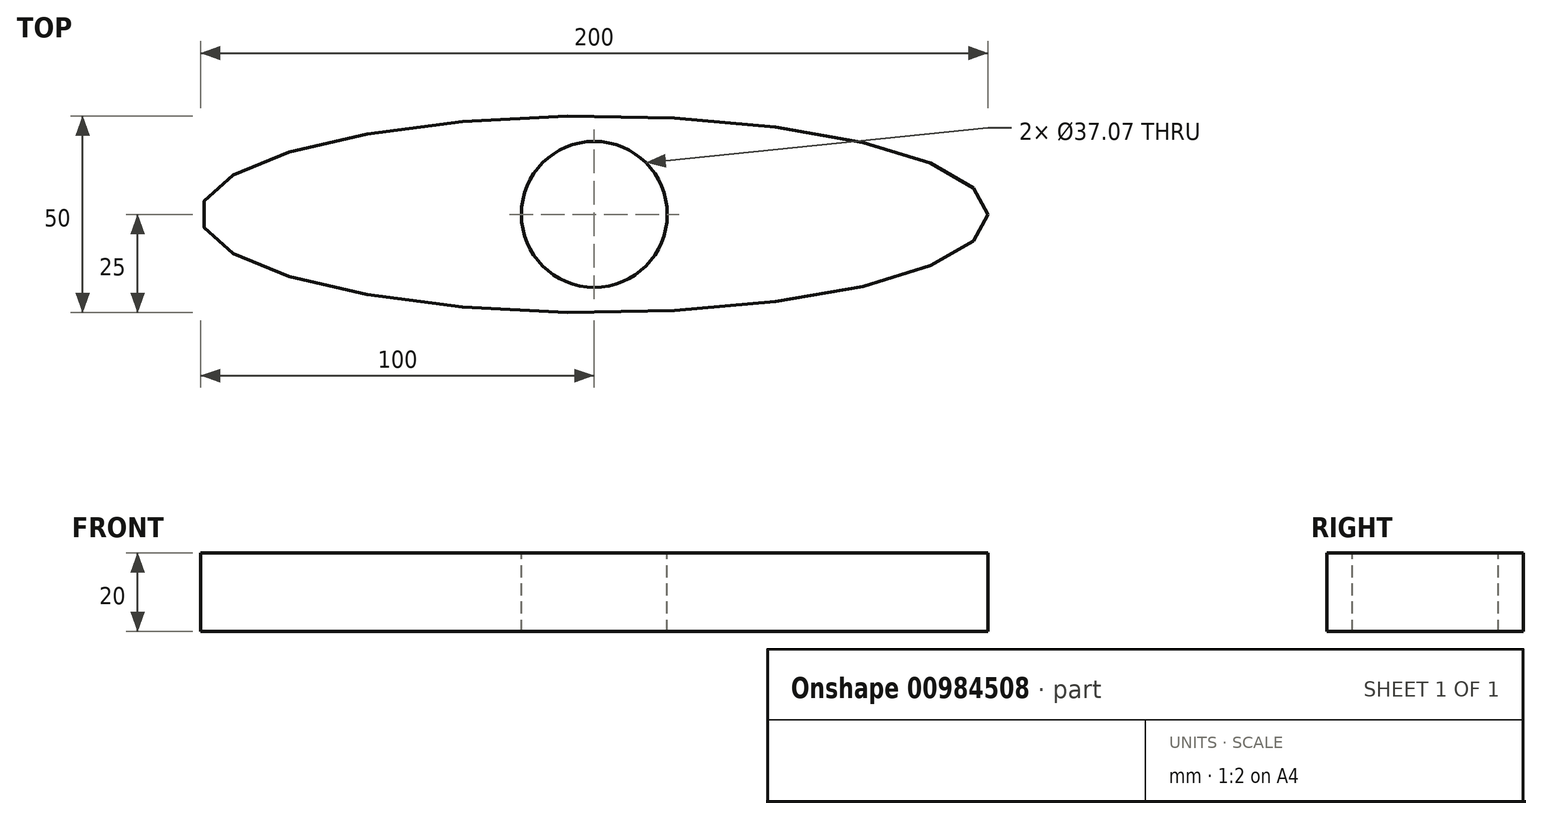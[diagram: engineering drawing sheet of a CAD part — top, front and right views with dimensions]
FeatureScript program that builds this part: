
annotation { "Feature Type Name" : "Feature", "Feature Type Description" : "" }
export const myFeature = defineFeature(function(context is Context, id is Id, definition is map)
    precondition{}
    {
        {
            var Q0;
            Q0=qCreatedBy(makeId("Top.planeOp"),FACE);
            var sketch = newSketch(context, id + "F0", { "sketchPlane" : qUnion([Q0])});
            skEllipse(sketch, "E0", {"center": v(0, 0) * mm, "majorRadius": 100 * mm, "minorRadius": 25 * mm, "majorAxis": v(1, 0)});
            skSolve(sketch);
        }
        {
            var Q0;
            Q0 = qSketchRegion(id + "F0", false);
            extrude(context, id + "F1", {"entities" : qUnion([Q0]), "depth" : 20 * mm});
        }
        {
            var Q0;
            Q0=qCreatedBy(makeId("Top.planeOp"),FACE);
            var sketch = newSketch(context, id + "F2", { "sketchPlane" : qUnion([Q0])});
            skEllipse(sketch, "E1", {"center": v(0, 0) * mm, "majorRadius": 100 * mm, "minorRadius": 25 * mm, "majorAxis": v(1, 0)});
            skSolve(sketch);
        }
        {
            var Q0;
            Q0 = qSketchRegion(id + "F2", false);
            extrude(context, id + "F3", {"entities" : qUnion([Q0]), "depth" : 20 * mm});
        }
        {
            var Q0;
            Q0=makeQuery(id+"F1.opExtrude","CAP_FACE",FACE,{"disambiguationData":[OSD([sQuery(id+"F0.wireOp",EDGE,"E0")])],"isStart":false});
            var sketch = newSketch(context, id + "F4", { "sketchPlane" : qUnion([Q0])});
            skCircle(sketch, "E2", {"center": v(0, 0) * mm, "radius": 18.53 * mm});
            skSolve(sketch);
        }
        {
            var Q0;
            Q0 = qSketchRegion(id + "F4", false);
            extrude(context, id + "F5", {"entities" : qUnion([Q0]), "operationType" : NewBodyOperationType.REMOVE, "depth" : 20 * mm, "oppositeDirection" : true});
        }
    });
